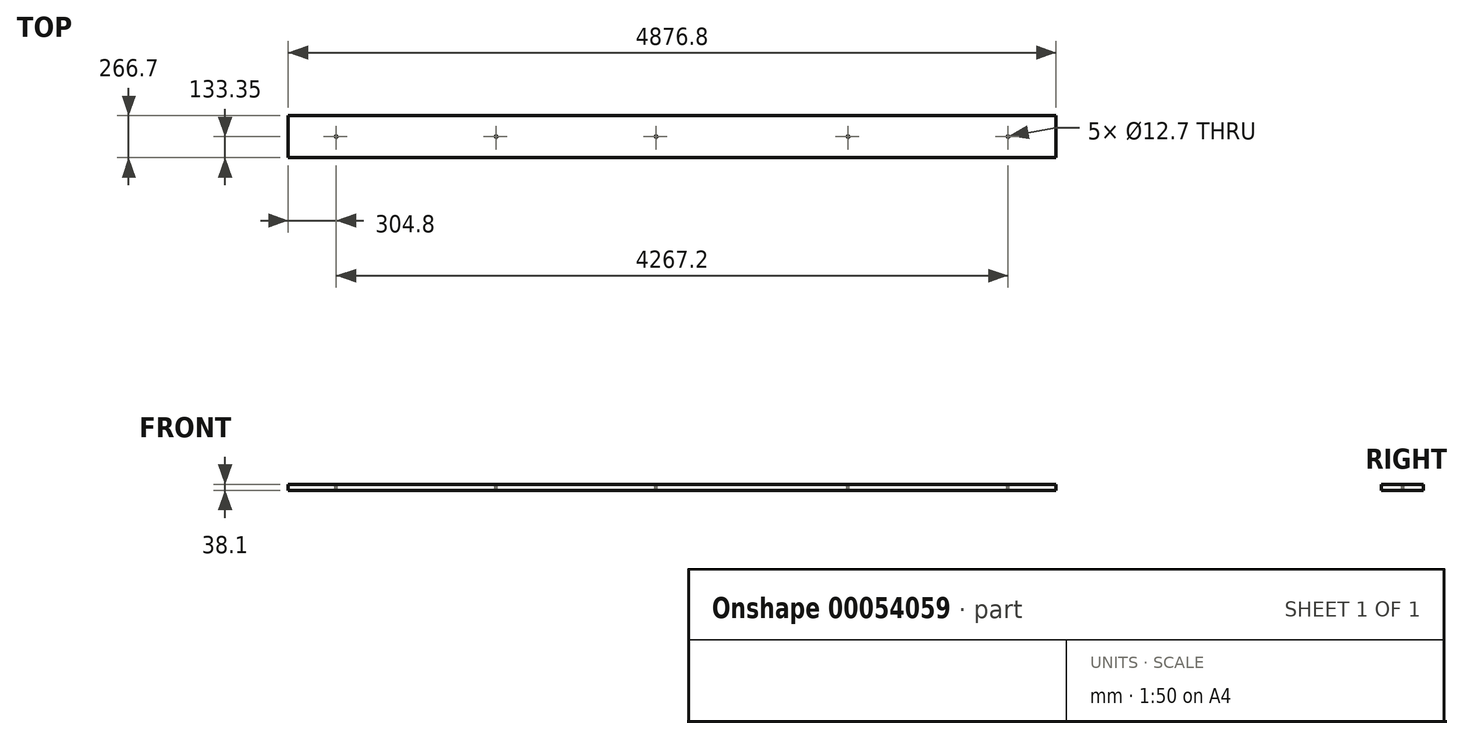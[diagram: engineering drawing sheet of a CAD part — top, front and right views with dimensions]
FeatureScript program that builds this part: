
annotation { "Feature Type Name" : "Feature", "Feature Type Description" : "" }
export const myFeature = defineFeature(function(context is Context, id is Id, definition is map)
    precondition{}
    {
        {
            var Q0;
            Q0=qCreatedBy(makeId("Right.planeOp"),FACE);
            var sketch = newSketch(context, id + "F0", { "sketchPlane" : qUnion([Q0])});
            skLineSegment(sketch, "E0.bottom", {"start": v(0, 0) * mm, "end": v(266.7, 0) * mm});
            skLineSegment(sketch, "E0.top", {"start": v(0, 38.1) * mm, "end": v(266.7, 38.1) * mm});
            skLineSegment(sketch, "E0.left", {"start": v(0, 0) * mm, "end": v(0, 38.1) * mm});
            skLineSegment(sketch, "E0.right", {"start": v(266.7, 0) * mm, "end": v(266.7, 38.1) * mm});
            skSolve(sketch);
        }
        {
            var Q0;
            Q0=makeQuery(id+"F0.imprint","IMPRINT",FACE,{"disambiguationData":[TD([[makeQuery(id+"F0.imprint","IMPRINT",EDGE,{"derivedFrom":sQuery(id+"F0.wireOp",EDGE,"E0.bottom")}),1.0]])]});
            extrude(context, id + "F1", {"entities" : qUnion([Q0]), "depth" : 4876.8 * mm});
        }
        {
            var Q0;
            Q0=makeQuery(id+"F1.opExtrude","SWEPT_FACE",FACE,{"disambiguationData":[OSD([sQuery(id+"F0.wireOp",EDGE,"E0.top")])]});
            var sketch = newSketch(context, id + "F2", { "sketchPlane" : qUnion([Q0])});
            skLineSegment(sketch, "E1", {"start": v(0, 133.35) * mm, "end": v(4876.8, 133.35) * mm, "construction": true});
            skCircle(sketch, "E2", {"center": v(304.8, 133.35) * mm, "radius": 6.35 * mm});
            skCircle(sketch, "E3", {"center": v(2336.8, 133.35) * mm, "radius": 6.35 * mm});
            skCircle(sketch, "E4", {"center": v(1320.8, 133.35) * mm, "radius": 6.35 * mm});
            skCircle(sketch, "E5", {"center": v(3556, 133.35) * mm, "radius": 6.35 * mm});
            skCircle(sketch, "E6", {"center": v(4572, 133.35) * mm, "radius": 6.35 * mm});
            skSolve(sketch);
        }
        {
            var Q0;
            Q0 = qSketchRegion(id + "F2", true);
            extrude(context, id + "F3", {"entities" : qUnion([Q0]), "operationType" : NewBodyOperationType.REMOVE, "endBound" : BoundingType.UP_TO_NEXT, "oppositeDirection" : true, "depth" : 25.4 * mm});
        }
    });
